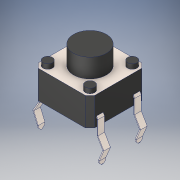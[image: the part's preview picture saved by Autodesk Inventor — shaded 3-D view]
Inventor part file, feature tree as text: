
AUTODESK INVENTOR PART (.ipt)
format: ipt  version: 2019.4 (Build 234330000, 330)  size: 186,880 bytes
history: mixed  units: mm
features: mirror x1, imported_body x1
ambient origin geometry x8: Origin, YZ Plane, XZ Plane, XY Plane, X Axis, Y Axis, Z Axis, Center Point
bodies: Solid1 (imported_parasolid)
feature tree (2):
  mirror  "Mirror3"
  imported_body  NMx_Import_Brep_tag  [imported B-rep: ~116 faces, bbox_mm=[7.565599, 8.48991, 6.01]]
